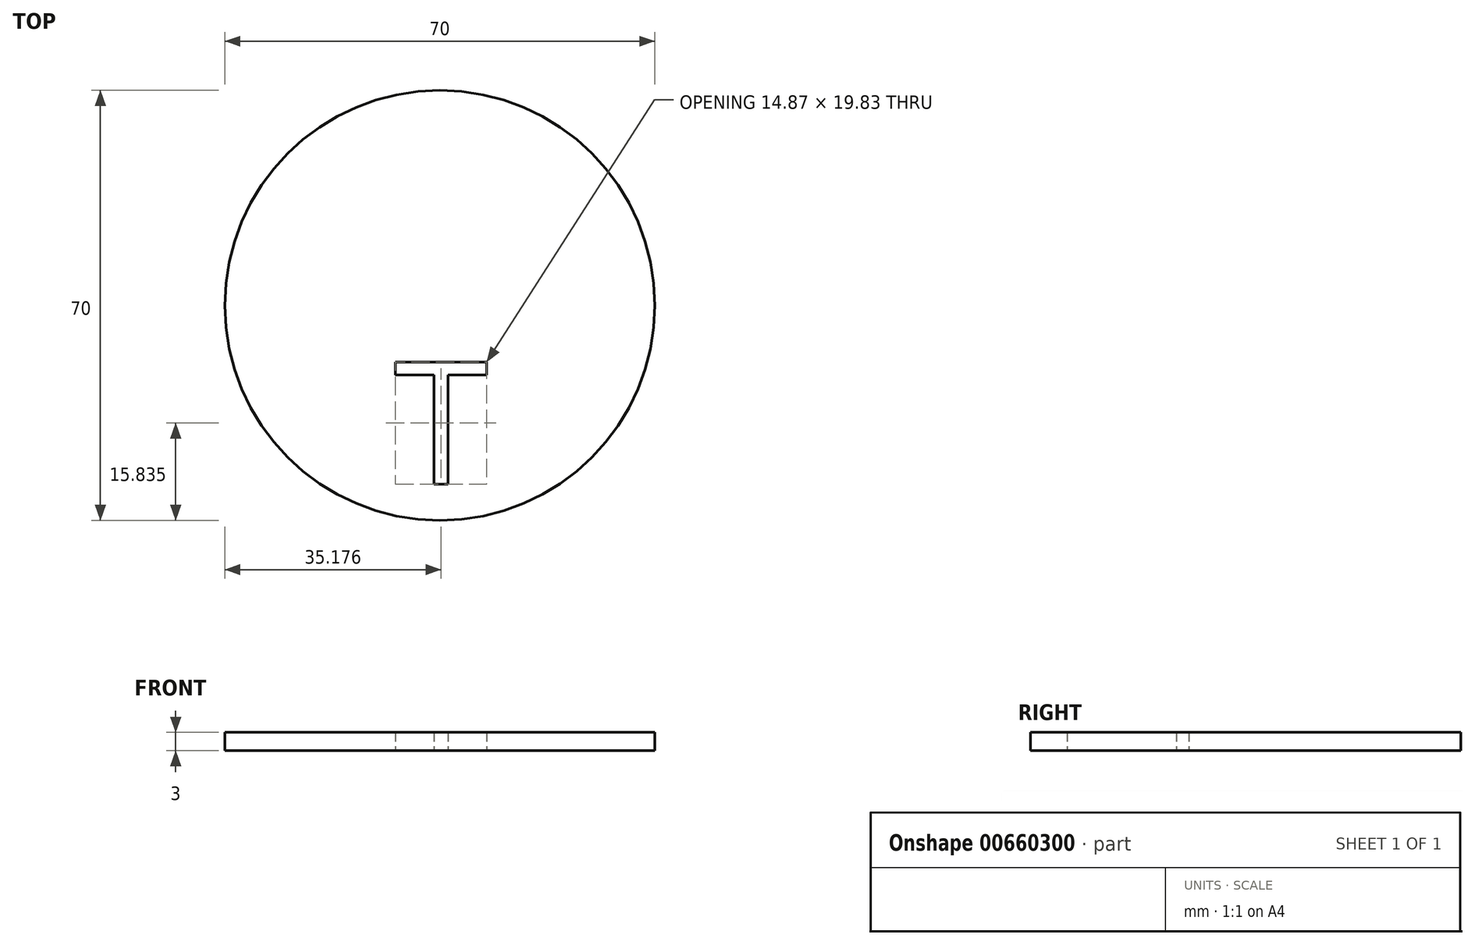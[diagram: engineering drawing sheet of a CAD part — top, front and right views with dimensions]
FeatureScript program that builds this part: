
annotation { "Feature Type Name" : "Feature", "Feature Type Description" : "" }
export const myFeature = defineFeature(function(context is Context, id is Id, definition is map)
    precondition{}
    {
        {
            var Q0;
            Q0=qCreatedBy(makeId("Top.planeOp"),FACE);
            var sketch = newSketch(context, id + "F0", { "sketchPlane" : qUnion([Q0])});
            skCircle(sketch, "E0", {"center": v(0, 0) * mm, "radius": 35 * mm});
            skText(sketch, "E1", { "text": "T", "fontName": "OpenSans-Regular.ttf"});
            skCircle(sketch, "E2", {"center": v(0, 0) * mm, "radius": 6 * mm, "construction": true});
            const initialGuessF0  = {"E1": [-0.0075, -0.02908, 1, 0, 0.02]};
            skSetInitialGuess(sketch, initialGuessF0);
            skSolve(sketch);
        }
        {
            var Q0;
            Q0 = qSketchRegion(id + "F0", true);
            extrude(context, id + "F1", {"entities" : qUnion([Q0]), "depth" : 3 * mm, "offsetDistance" : 25 * mm});
        }
    });
